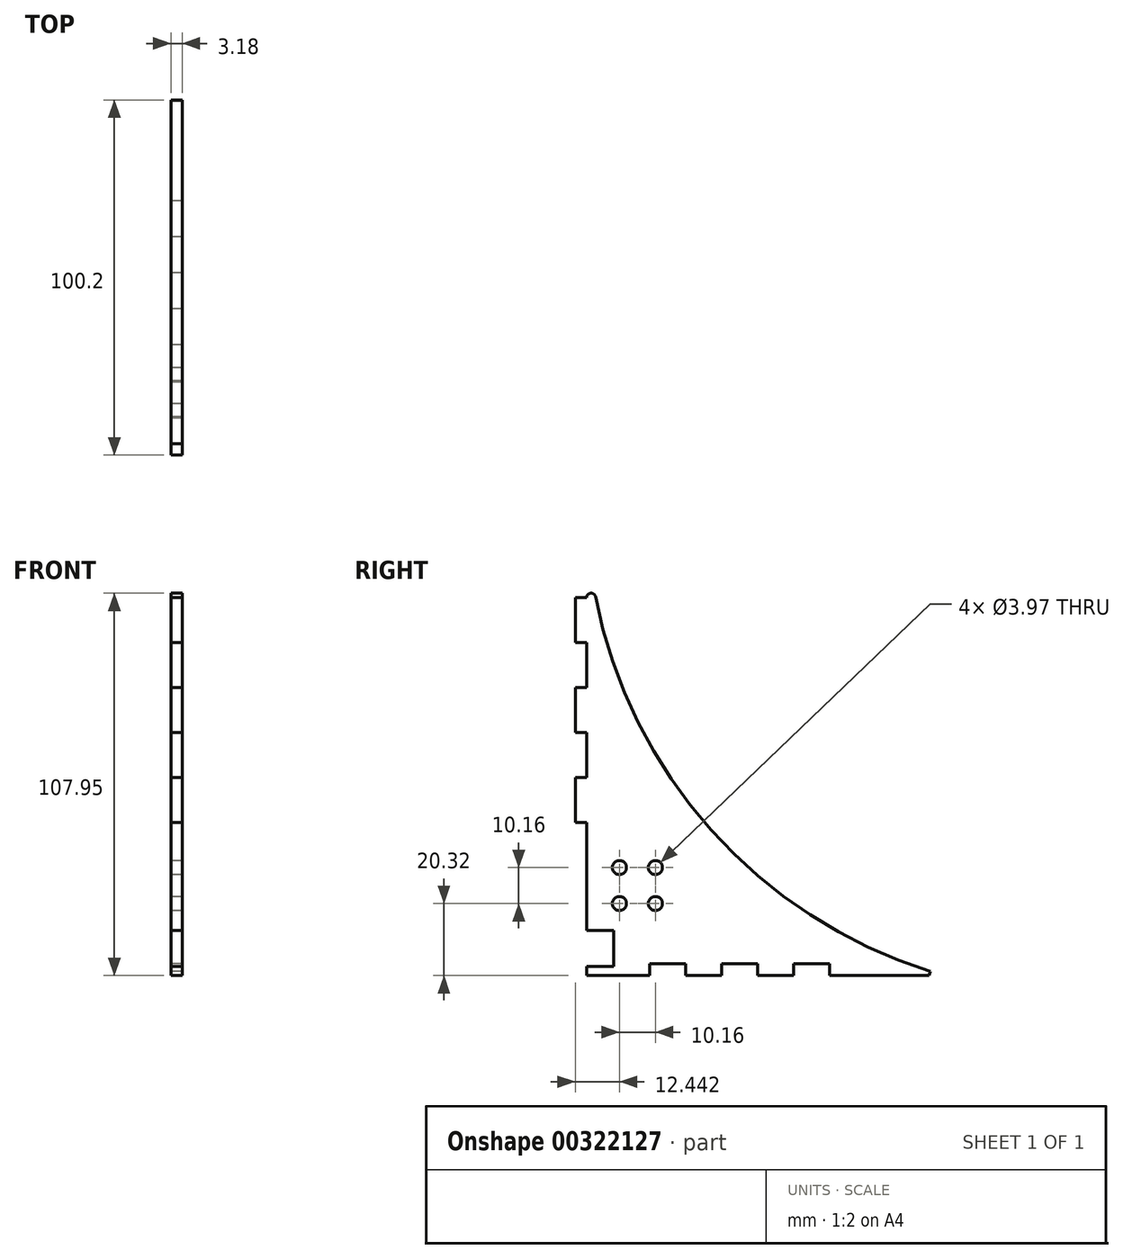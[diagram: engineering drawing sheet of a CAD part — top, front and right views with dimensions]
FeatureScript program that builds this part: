
annotation { "Feature Type Name" : "Feature", "Feature Type Description" : "" }
export const myFeature = defineFeature(function(context is Context, id is Id, definition is map)
    precondition{}
    {
        {
            var Q0;
            Q0=qCreatedBy(makeId("Right.planeOp"),FACE);
            var sketch = newSketch(context, id + "F0", { "sketchPlane" : qUnion([Q0])});
            skLineSegment(sketch, "E0", {"start": v(-51.38, 38.1) * mm, "end": v(-51.38, -73.66) * mm});
            skLineSegment(sketch, "E1", {"start": v(-51.38, -73.66) * mm, "end": v(60.38, -73.66) * mm});
            skArc(sketch, "E2", {"start": v(-48.86, 38.34) * mm, "mid": v(-10.88, -33.16) * mm, "end": v(60.62, -71.14) * mm});
            skPoint(sketch, "E3.visualSharp", {"position": v(86.88, -73.66) * mm});
            skPoint(sketch, "E4.visualSharp", {"position": v(-51.38, 64.6) * mm});
            skArc(sketch, "E4.filletArc", {"start": v(-48.86, 38.34) * mm, "mid": v(-50.23, 39.36) * mm, "end": v(-51.38, 38.1) * mm});
            skLineSegment(sketch, "E5", {"start": v(-51.38, 38.1) * mm, "end": v(-54.55, 38.1) * mm});
            skLineSegment(sketch, "E6", {"start": v(-54.55, 38.1) * mm, "end": v(-54.55, 25.4) * mm});
            skLineSegment(sketch, "E7", {"start": v(-54.55, 25.4) * mm, "end": v(-51.38, 25.4) * mm});
            skLineSegment(sketch, "E8", {"start": v(-51.38, 12.7) * mm, "end": v(-54.55, 12.7) * mm});
            skLineSegment(sketch, "E9", {"start": v(-54.55, 12.7) * mm, "end": v(-54.55, 0) * mm});
            skLineSegment(sketch, "E10", {"start": v(-54.55, 0) * mm, "end": v(-51.38, 0) * mm});
            skLineSegment(sketch, "E11", {"start": v(-51.38, -12.7) * mm, "end": v(-54.55, -12.7) * mm});
            skLineSegment(sketch, "E12", {"start": v(-54.55, -12.7) * mm, "end": v(-54.55, -25.4) * mm});
            skLineSegment(sketch, "E13", {"start": v(-54.55, -25.4) * mm, "end": v(-51.38, -25.4) * mm});
            skLineSegment(sketch, "E14", {"start": v(-54.55, 25.4) * mm, "end": v(-54.55, 12.7) * mm, "construction": true});
            skLineSegment(sketch, "E15", {"start": v(-54.55, 0) * mm, "end": v(-54.55, -12.7) * mm, "construction": true});
            skLineSegment(sketch, "E16.bottom", {"start": v(-51.38, -73.66) * mm, "end": v(-43.76, -73.66) * mm});
            skLineSegment(sketch, "E16.top", {"start": v(-51.38, -66.04) * mm, "end": v(-43.76, -66.04) * mm});
            skLineSegment(sketch, "E16.left", {"start": v(-51.38, -73.66) * mm, "end": v(-51.38, -66.04) * mm});
            skLineSegment(sketch, "E17", {"start": v(-43.76, -66.04) * mm, "end": v(-43.76, -55.88) * mm});
            skLineSegment(sketch, "E18", {"start": v(-43.76, -55.88) * mm, "end": v(-51.38, -55.88) * mm});
            skArc(sketch, "E19", {"start": v(60.62, -71.14) * mm, "mid": v(62.25, -71.96) * mm, "end": v(62.9, -73.66) * mm});
            skLineSegment(sketch, "E20", {"start": v(60.38, -73.66) * mm, "end": v(62.9, -73.66) * mm});
            skLineSegment(sketch, "E21", {"start": v(-51.38, -68.58) * mm, "end": v(49.75, -68.58) * mm});
            skPoint(sketch, "E22", {"position": v(45.27, -68.58) * mm});
            skArc(sketch, "E23", {"start": v(46.54, -68.58) * mm, "mid": v(46.3, -67.83) * mm, "end": v(45.65, -67.37) * mm});
            skLineSegment(sketch, "E24", {"start": v(45.27, -68.58) * mm, "end": v(45.65, -67.37) * mm});
            skLineSegment(sketch, "E25", {"start": v(-33.6, -68.58) * mm, "end": v(-33.6, -65.28) * mm});
            skLineSegment(sketch, "E26", {"start": v(-33.6, -65.28) * mm, "end": v(-23.44, -65.28) * mm});
            skLineSegment(sketch, "E27", {"start": v(-23.44, -65.28) * mm, "end": v(-23.44, -68.58) * mm});
            skLineSegment(sketch, "E28", {"start": v(-13.28, -68.58) * mm, "end": v(-13.28, -65.28) * mm});
            skLineSegment(sketch, "E29", {"start": v(-13.28, -65.28) * mm, "end": v(-3.12, -65.28) * mm});
            skLineSegment(sketch, "E30", {"start": v(-3.12, -65.28) * mm, "end": v(-3.12, -68.58) * mm});
            skLineSegment(sketch, "E31", {"start": v(7.04, -68.58) * mm, "end": v(7.04, -65.28) * mm});
            skLineSegment(sketch, "E32", {"start": v(7.04, -65.28) * mm, "end": v(17.2, -65.28) * mm});
            skLineSegment(sketch, "E33", {"start": v(17.2, -65.28) * mm, "end": v(17.2, -68.58) * mm});
            skCircle(sketch, "E34", {"center": v(-42.1, -38.1) * mm, "radius": 1.98 * mm});
            skCircle(sketch, "E35.0.1.0", {"center": v(-42.1, -48.26) * mm, "radius": 1.98 * mm});
            skCircle(sketch, "E35.1.0.0", {"center": v(-31.95, -38.1) * mm, "radius": 1.98 * mm});
            skCircle(sketch, "E35.1.1.0", {"center": v(-31.95, -48.26) * mm, "radius": 1.98 * mm});
            skLineSegment(sketch, "E35.direction1", {"start": v(-42.1, -38.1) * mm, "end": v(-31.95, -38.1) * mm, "construction": true});
            skLineSegment(sketch, "E35.direction2", {"start": v(-42.1, -38.1) * mm, "end": v(-42.1, -48.26) * mm, "construction": true});
            skSolve(sketch);
        }
        {
            var Q0;
            {var subQ0=sQuery(id+"F0.wireOp",EDGE,"E5");Q0=makeQuery(id+"F0.imprint","IMPRINT",FACE,{"disambiguationData":[TD([[makeQuery(id+"F0.imprint","IMPRINT",EDGE,{"derivedFrom":subQ0}),1.0]])]});}
            var Q1;
            {var subQ0=sQuery(id+"F0.wireOp",EDGE,"E8");Q1=makeQuery(id+"F0.imprint","IMPRINT",FACE,{"disambiguationData":[TD([[makeQuery(id+"F0.imprint","IMPRINT",EDGE,{"derivedFrom":subQ0}),1.0]])]});}
            var Q2;
            {var subQ0=sQuery(id+"F0.wireOp",EDGE,"E11");Q2=makeQuery(id+"F0.imprint","IMPRINT",FACE,{"disambiguationData":[TD([[makeQuery(id+"F0.imprint","IMPRINT",EDGE,{"derivedFrom":subQ0}),1.0]])]});}
            var Q3;
            {var subQ1=sQuery(id+"F0.wireOp",EDGE,"E4.filletArc");Q3=makeQuery(id+"F0.imprint","IMPRINT",FACE,{"disambiguationData":[TD([[makeQuery(id+"F0.imprint","IMPRINT",EDGE,{"derivedFrom":subQ1}),1.0]])]});}
            extrude(context, id + "F1", {"entities" : qUnion([Q0, Q1, Q2, Q3]), "depth" : 3.17 * mm});
        }
    });
